# Revit family: 306_H7_R
name_source: partatom
category: Pipe Accessories
units: mm (PartAtom-declared; Revit-internal decimal feet)

## family parameters
Always vertical = Yes
Cut with Voids When Loaded = No
Part Type = Valve - Breaks Into
Round Connector Dimension = Use Diameter
Shared = No
Work Plane-Based = No

## types (13) — shared parameters
CAT0 = Yes
Description = Globe valve, 3-way, Flange, PN 6
L2D_Min = 3048 mm
Manufacturer = Belimo
QmdConnectorList = 301;D;302;D;303;D
magiPartTypeId = 306
magiProductFamilyId = H7*R
zero-valued in all types: MC_Default_elevation

## per-type parameters (varying)
| type | BB | BB1 | C | C__ve | D | DB1 | DB2 | DB3 | DB4 | FD | H | HH1 | L2 | L2D | LM | W2D |
| H711R | 26 mm | 20 mm  [stored 0.0656168 ft] | 12 mm  [stored 0.0393701 ft] | -12 mm  [stored -0.0393701 ft] | 15 mm | 32 mm  [stored 0.104987 ft] | 64 mm  [stored 0.209974 ft] | 29 mm | 51 mm | 80 mm  [stored 0.262467 ft] | 65 mm  [stored 0.213255 ft] | 21 mm | 65 mm  [stored 0.213255 ft] | 130 mm | 106 mm | 15 mm  [stored 0.0492126 ft] |
| H7100R | 71 mm | 54 mm | 18 mm  [stored 0.0590551 ft] | -18 mm  [stored -0.0590551 ft] | 100 mm | 126 mm | 252 mm | 113 mm | 202 mm | 210 mm | 150 mm | 57 mm  [stored 0.187008 ft] | 175 mm | 350 mm | 314 mm | 100 mm |
| H779R | 71 mm | 54 mm | 18 mm  [stored 0.0590551 ft] | -18 mm  [stored -0.0590551 ft] | 80 mm | 126 mm | 252 mm | 113 mm | 202 mm | 210 mm | 150 mm | 57 mm  [stored 0.187008 ft] | 155 mm | 310 mm | 274 mm | 80 mm  [stored 0.262467 ft] |
| H764R | 57 mm  [stored 0.187008 ft] | 43 mm  [stored 0.141076 ft] | 16 mm  [stored 0.0524934 ft] | -16 mm  [stored -0.0524934 ft] | 65 mm | 80 mm  [stored 0.262467 ft] | 160 mm | 72 mm  [stored 0.23622 ft] | 128 mm | 160 mm | 120 mm | 44 mm  [stored 0.144357 ft] | 145 mm | 290 mm | 258 mm | 65 mm  [stored 0.213255 ft] |
| H750R | 36 mm  [stored 0.11811 ft] | 28 mm | 16 mm  [stored 0.0524934 ft] | -16 mm  [stored -0.0524934 ft] | 50 mm | 56 mm  [stored 0.183727 ft] | 112 mm | 50 mm  [stored 0.164042 ft] | 90 mm  [stored 0.295276 ft] | 140 mm | 100 mm | 34 mm  [stored 0.111549 ft] | 115 mm | 230 mm | 198 mm | 50 mm  [stored 0.164042 ft] |
| H740R | 36 mm  [stored 0.11811 ft] | 28 mm | 16 mm  [stored 0.0524934 ft] | -16 mm  [stored -0.0524934 ft] | 40 mm | 52 mm  [stored 0.170604 ft] | 104 mm | 47 mm | 83 mm | 130 mm | 100 mm | 34 mm  [stored 0.111549 ft] | 100 mm | 200 mm | 168 mm | 40 mm  [stored 0.131234 ft] |
| H732R | 32 mm  [stored 0.104987 ft] | 24 mm | 16 mm  [stored 0.0524934 ft] | -16 mm  [stored -0.0524934 ft] | 32 mm | 52 mm  [stored 0.170604 ft] | 104 mm | 47 mm | 83 mm | 130 mm | 95 mm | 32 mm  [stored 0.104987 ft] | 90 mm  [stored 0.295276 ft] | 180 mm | 148 mm | 32 mm  [stored 0.104987 ft] |
| H725R | 30 mm  [stored 0.0984252 ft] | 22 mm | 14 mm  [stored 0.0459318 ft] | -14 mm  [stored -0.0459318 ft] | 25 mm | 40 mm  [stored 0.131234 ft] | 80 mm  [stored 0.262467 ft] | 36 mm  [stored 0.11811 ft] | 64 mm  [stored 0.209974 ft] | 100 mm | 75 mm  [stored 0.246063 ft] | 24 mm | 80 mm  [stored 0.262467 ft] | 160 mm | 132 mm | 25 mm  [stored 0.082021 ft] |
| H720R | 30 mm  [stored 0.0984252 ft] | 22 mm | 14 mm  [stored 0.0459318 ft] | -14 mm  [stored -0.0459318 ft] | 20 mm | 40 mm  [stored 0.131234 ft] | 80 mm  [stored 0.262467 ft] | 36 mm  [stored 0.11811 ft] | 64 mm  [stored 0.209974 ft] | 100 mm | 75 mm  [stored 0.246063 ft] | 24 mm | 75 mm  [stored 0.246063 ft] | 150 mm | 122 mm | 20 mm  [stored 0.0656168 ft] |
| H715R | 26 mm | 20 mm  [stored 0.0656168 ft] | 12 mm  [stored 0.0393701 ft] | -12 mm  [stored -0.0393701 ft] | 15 mm | 32 mm  [stored 0.104987 ft] | 64 mm  [stored 0.209974 ft] | 29 mm | 51 mm | 80 mm  [stored 0.262467 ft] | 65 mm  [stored 0.213255 ft] | 21 mm | 65 mm  [stored 0.213255 ft] | 130 mm | 106 mm | 15 mm  [stored 0.0492126 ft] |
| H714R | 26 mm | 20 mm  [stored 0.0656168 ft] | 12 mm  [stored 0.0393701 ft] | -12 mm  [stored -0.0393701 ft] | 15 mm | 32 mm  [stored 0.104987 ft] | 64 mm  [stored 0.209974 ft] | 29 mm | 51 mm | 80 mm  [stored 0.262467 ft] | 65 mm  [stored 0.213255 ft] | 21 mm | 65 mm  [stored 0.213255 ft] | 130 mm | 106 mm | 15 mm  [stored 0.0492126 ft] |
| H713R | 26 mm | 20 mm  [stored 0.0656168 ft] | 12 mm  [stored 0.0393701 ft] | -12 mm  [stored -0.0393701 ft] | 15 mm | 32 mm  [stored 0.104987 ft] | 64 mm  [stored 0.209974 ft] | 29 mm | 51 mm | 80 mm  [stored 0.262467 ft] | 65 mm  [stored 0.213255 ft] | 21 mm | 65 mm  [stored 0.213255 ft] | 130 mm | 106 mm | 15 mm  [stored 0.0492126 ft] |
| H712R | 26 mm | 20 mm  [stored 0.0656168 ft] | 12 mm  [stored 0.0393701 ft] | -12 mm  [stored -0.0393701 ft] | 15 mm | 32 mm  [stored 0.104987 ft] | 64 mm  [stored 0.209974 ft] | 29 mm | 51 mm | 80 mm  [stored 0.262467 ft] | 65 mm  [stored 0.213255 ft] | 21 mm | 65 mm  [stored 0.213255 ft] | 130 mm | 106 mm | 15 mm  [stored 0.0492126 ft] |

note: column(s) folded — value = type name in every type: magiProductCode, magiProductId

note: [stored X ft] marks values corroborated as IEEE doubles in the binary element streams (Revit-internal decimal feet)

## geometry (parser evidence)
native form markers: Sweep x2
no freeform markers — native parametric forms only
